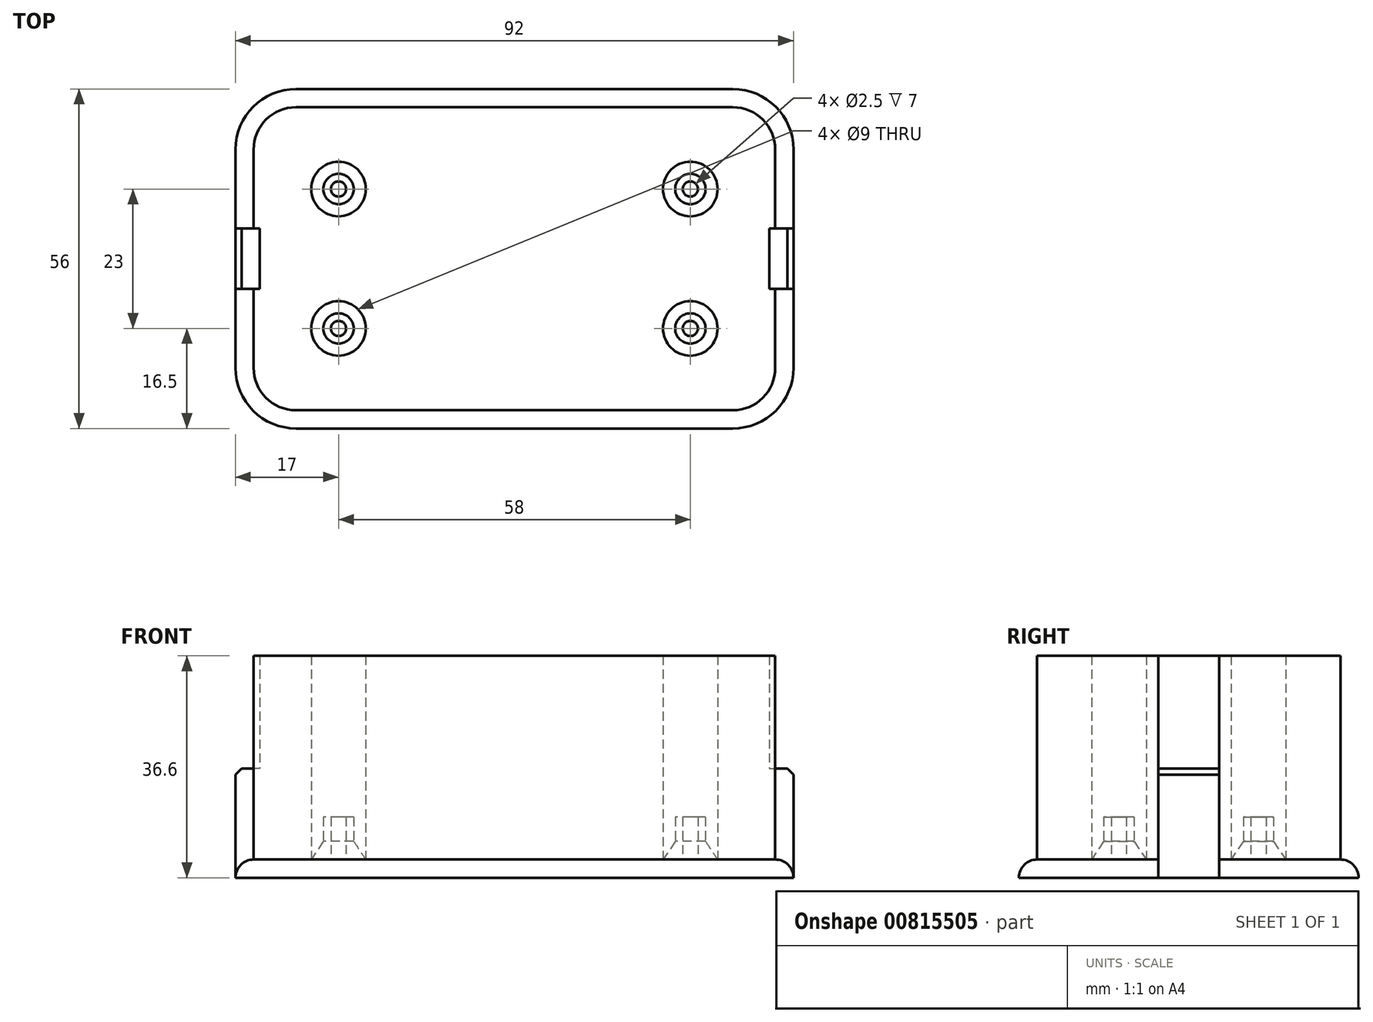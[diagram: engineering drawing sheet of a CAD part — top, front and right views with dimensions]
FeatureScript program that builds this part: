
annotation { "Feature Type Name" : "Feature", "Feature Type Description" : "" }
export const myFeature = defineFeature(function(context is Context, id is Id, definition is map)
    precondition{}
    {
        {
            var Q0;
            Q0=qCreatedBy(makeId("Top.planeOp"),FACE);
            var sketch = newSketch(context, id + "F0", { "sketchPlane" : qUnion([Q0])});
            skLineSegment(sketch, "E0.bottom", {"start": v(36, 28) * mm, "end": v(-36, 28) * mm});
            skLineSegment(sketch, "E0.top", {"start": v(36, -28) * mm, "end": v(-36, -28) * mm});
            skLineSegment(sketch, "E0.left", {"start": v(46, 18) * mm, "end": v(46, -18) * mm});
            skLineSegment(sketch, "E0.right", {"start": v(-46, 18) * mm, "end": v(-46, -18) * mm});
            skPoint(sketch, "E0.middle", {"position": v(0, 0) * mm});
            skPoint(sketch, "E1.visualSharp", {"position": v(-46, 28) * mm});
            skArc(sketch, "E1.filletArc", {"start": v(-36, 28) * mm, "mid": v(-43.07, 25.07) * mm, "end": v(-46, 18) * mm});
            skPoint(sketch, "E2.visualSharp", {"position": v(-46, -28) * mm});
            skArc(sketch, "E2.filletArc", {"start": v(-46, -18) * mm, "mid": v(-43.07, -25.07) * mm, "end": v(-36, -28) * mm});
            skPoint(sketch, "E3.visualSharp", {"position": v(46, -28) * mm});
            skArc(sketch, "E3.filletArc", {"start": v(36, -28) * mm, "mid": v(43.07, -25.07) * mm, "end": v(46, -18) * mm});
            skPoint(sketch, "E4.visualSharp", {"position": v(46, 28) * mm});
            skArc(sketch, "E4.filletArc", {"start": v(46, 18) * mm, "mid": v(43.07, 25.07) * mm, "end": v(36, 28) * mm});
            skSolve(sketch);
        }
        {
            var Q0;
            Q0=qCreatedBy(makeId("Top.planeOp"),FACE);
            var sketch = newSketch(context, id + "F1", { "sketchPlane" : qUnion([Q0])});
            skPoint(sketch, "E5", {"position": v(-32.5, 15) * mm});
            skPoint(sketch, "E6", {"position": v(32.5, 15) * mm});
            skPoint(sketch, "E7", {"position": v(32.5, -15) * mm});
            skPoint(sketch, "E8", {"position": v(-32.5, -15) * mm});
            skLineSegment(sketch, "E9", {"start": v(-29.5, 15) * mm, "end": v(29.5, 15) * mm, "construction": true});
            skLineSegment(sketch, "E10", {"start": v(32.5, 12) * mm, "end": v(32.5, -12) * mm, "construction": true});
            skLineSegment(sketch, "E11.MirrorCS", {"start": v(-29.5, -15) * mm, "end": v(29.5, -15) * mm, "construction": true});
            skLineSegment(sketch, "E12.MirrorCS", {"start": v(-32.5, 12) * mm, "end": v(-32.5, -12) * mm, "construction": true});
            skArc(sketch, "E13.filletArc", {"start": v(32.5, 12) * mm, "mid": v(31.62, 14.12) * mm, "end": v(29.5, 15) * mm, "construction": true});
            skArc(sketch, "E14.filletArc", {"start": v(-29.5, 15) * mm, "mid": v(-31.62, 14.12) * mm, "end": v(-32.5, 12) * mm, "construction": true});
            skArc(sketch, "E15.filletArc", {"start": v(-32.5, -12) * mm, "mid": v(-31.62, -14.12) * mm, "end": v(-29.5, -15) * mm, "construction": true});
            skArc(sketch, "E16.filletArc", {"start": v(29.5, -15) * mm, "mid": v(31.62, -14.12) * mm, "end": v(32.5, -12) * mm, "construction": true});
            skCircle(sketch, "E17", {"center": v(-29, 11.5) * mm, "radius": 1.25 * mm});
            skCircle(sketch, "E18.MirrorC", {"center": v(29, 11.5) * mm, "radius": 1.25 * mm});
            skCircle(sketch, "E19.MirrorC", {"center": v(-29, -11.5) * mm, "radius": 1.25 * mm});
            skCircle(sketch, "E20.MirrorC", {"center": v(29, -11.5) * mm, "radius": 1.25 * mm});
            skCircle(sketch, "E21", {"center": v(-29, 11.5) * mm, "radius": 2.5 * mm});
            skCircle(sketch, "E22.MirrorC", {"center": v(29, 11.5) * mm, "radius": 2.5 * mm});
            skCircle(sketch, "E23.MirrorC", {"center": v(-29, -11.5) * mm, "radius": 2.5 * mm});
            skCircle(sketch, "E24.MirrorC", {"center": v(29, -11.5) * mm, "radius": 2.5 * mm});
            skSolve(sketch);
        }
        {
            var Q0;
            Q0=makeQuery(id+"F0.imprint","IMPRINT",FACE,{"disambiguationData":[TD([[makeQuery(id+"F0.imprint","IMPRINT",EDGE,{"derivedFrom":sQuery(id+"F0.wireOp",EDGE,"E0.bottom")}),1.0]])]});
            extrude(context, id + "F2", {"entities" : qUnion([Q0]), "depth" : 3 * mm, "offsetDistance" : 25 * mm});
        }
        {
            var Q0;
            Q0=qSketchRegion(id+"F1",true);
            extrude(context, id + "F3", {"entities" : qUnion([Q0]), "operationType" : NewBodyOperationType.ADD, "depth" : 10 * mm, "offsetDistance" : 25 * mm});
        }
        {
            var Q0;
            Q0=makeQuery(id+"F3.boolean.opBoolean","INTERSECT",EDGE,{"derivedFrom":[makeQuery(id+"F2.opExtrude","CAP_FACE",FACE,{"disambiguationData":[OSD([sQuery(id+"F0.wireOp",EDGE,"E0.bottom"),sQuery(id+"F0.wireOp",EDGE,"E0.top"),sQuery(id+"F0.wireOp",EDGE,"E0.left"),sQuery(id+"F0.wireOp",EDGE,"E0.right"),sQuery(id+"F0.wireOp",EDGE,"E1.filletArc"),sQuery(id+"F0.wireOp",EDGE,"E2.filletArc"),sQuery(id+"F0.wireOp",EDGE,"E3.filletArc"),sQuery(id+"F0.wireOp",EDGE,"E4.filletArc")])],"isStart":false}),makeQuery(id+"F3.opExtrude","SWEPT_FACE",FACE,{"disambiguationData":[OSD([sQuery(id+"F1.wireOp",EDGE,"E21")])]})]});
            var Q1;
            Q1=makeQuery(id+"F3.boolean.opBoolean","INTERSECT",EDGE,{"derivedFrom":[makeQuery(id+"F2.opExtrude","CAP_FACE",FACE,{"disambiguationData":[OSD([sQuery(id+"F0.wireOp",EDGE,"E0.bottom"),sQuery(id+"F0.wireOp",EDGE,"E0.top"),sQuery(id+"F0.wireOp",EDGE,"E0.left"),sQuery(id+"F0.wireOp",EDGE,"E0.right"),sQuery(id+"F0.wireOp",EDGE,"E1.filletArc"),sQuery(id+"F0.wireOp",EDGE,"E2.filletArc"),sQuery(id+"F0.wireOp",EDGE,"E3.filletArc"),sQuery(id+"F0.wireOp",EDGE,"E4.filletArc")])],"isStart":false}),makeQuery(id+"F3.opExtrude","SWEPT_FACE",FACE,{"disambiguationData":[OSD([sQuery(id+"F1.wireOp",EDGE,"E22.MirrorC")])]})]});
            var Q2;
            Q2=makeQuery(id+"F3.boolean.opBoolean","INTERSECT",EDGE,{"derivedFrom":[makeQuery(id+"F2.opExtrude","CAP_FACE",FACE,{"disambiguationData":[OSD([sQuery(id+"F0.wireOp",EDGE,"E0.bottom"),sQuery(id+"F0.wireOp",EDGE,"E0.top"),sQuery(id+"F0.wireOp",EDGE,"E0.left"),sQuery(id+"F0.wireOp",EDGE,"E0.right"),sQuery(id+"F0.wireOp",EDGE,"E1.filletArc"),sQuery(id+"F0.wireOp",EDGE,"E2.filletArc"),sQuery(id+"F0.wireOp",EDGE,"E3.filletArc"),sQuery(id+"F0.wireOp",EDGE,"E4.filletArc")])],"isStart":false}),makeQuery(id+"F3.opExtrude","SWEPT_FACE",FACE,{"disambiguationData":[OSD([sQuery(id+"F1.wireOp",EDGE,"E24.MirrorC")])]})]});
            var Q3;
            Q3=makeQuery(id+"F3.boolean.opBoolean","INTERSECT",EDGE,{"derivedFrom":[makeQuery(id+"F2.opExtrude","CAP_FACE",FACE,{"disambiguationData":[OSD([sQuery(id+"F0.wireOp",EDGE,"E0.bottom"),sQuery(id+"F0.wireOp",EDGE,"E0.top"),sQuery(id+"F0.wireOp",EDGE,"E0.left"),sQuery(id+"F0.wireOp",EDGE,"E0.right"),sQuery(id+"F0.wireOp",EDGE,"E1.filletArc"),sQuery(id+"F0.wireOp",EDGE,"E2.filletArc"),sQuery(id+"F0.wireOp",EDGE,"E3.filletArc"),sQuery(id+"F0.wireOp",EDGE,"E4.filletArc")])],"isStart":false}),makeQuery(id+"F3.opExtrude","SWEPT_FACE",FACE,{"disambiguationData":[OSD([sQuery(id+"F1.wireOp",EDGE,"E23.MirrorC")])]})]});
            chamfer(context, id + "F4", {"entities" : qUnion([Q0, Q1, Q2, Q3]), "chamferType" : ChamferType.TWO_OFFSETS, "width1" : 2 * mm, "oppositeDirection" : false, "width2" : 3 * mm, "tangentPropagation" : true});
        }
        {
            var Q0;
            Q0=makeQuery(id+"F2.opExtrude","CAP_EDGE",EDGE,{"disambiguationData":[OSD([sQuery(id+"F0.wireOp",EDGE,"E0.bottom")])],"isStart":false});
            fillet(context, id + "F5", {"entities" : qUnion([Q0]), "radius" : 3 * mm, "tangentPropagation" : true, "allowEdgeOverflow" : false});
        }
        {
            var Q0;
            Q0=qCreatedBy(makeId("Right.planeOp"),FACE);
            cPlane(context, id + "F6", {"entities" : qUnion([Q0]), "cplaneType" : CPlaneType.OFFSET, "offset" : 46 * mm, "width" : 150 * mm, "height" : 150 * mm});
        }
        {
            var Q0;
            Q0=qCreatedBy(id+"F6.planeOp",FACE);
            var sketch = newSketch(context, id + "F7", { "sketchPlane" : qUnion([Q0])});
            skLineSegment(sketch, "E25", {"start": v(-5, 0) * mm, "end": v(-5, 18) * mm});
            skLineSegment(sketch, "E26", {"start": v(-5, 18) * mm, "end": v(5, 18) * mm});
            skLineSegment(sketch, "E27", {"start": v(5, 18) * mm, "end": v(5, 0) * mm});
            skLineSegment(sketch, "E28", {"start": v(-5, 0) * mm, "end": v(5, 0) * mm});
            skSolve(sketch);
        }
        {
            var Q0;
            Q0=makeQuery(id+"F7.imprint","IMPRINT",FACE,{"disambiguationData":[TD([[makeQuery(id+"F7.imprint","IMPRINT",EDGE,{"derivedFrom":sQuery(id+"F7.wireOp",EDGE,"E25")}),-1.0]])]});
            extrude(context, id + "F8", {"entities" : qUnion([Q0]), "oppositeDirection" : true, "depth" : 4 * mm, "offsetDistance" : 25 * mm});
        }
        {
            var Q0;
            Q0=makeQuery(id+"F8.opExtrude","SWEPT_BODY",BODY,{"disambiguationData":[OSD([sQuery(id+"F7.wireOp",EDGE,"E25"),sQuery(id+"F7.wireOp",EDGE,"E26"),sQuery(id+"F7.wireOp",EDGE,"E27"),sQuery(id+"F7.wireOp",EDGE,"E28")])]});
            var Q1;
            Q1=qCreatedBy(makeId("Right.planeOp"),FACE);
            mirror(context, id + "F9", {"operationType" : NewBodyOperationType.ADD, "entities" : qUnion([Q0]), "mirrorPlane" : qUnion([Q1])});
        }
        {
            var Q0;
            Q0=makeQuery(id+"F9.opPattern","COPY",EDGE,{"derivedFrom":makeQuery(id+"F8.opExtrude","CAP_EDGE",EDGE,{"disambiguationData":[OSD([sQuery(id+"F7.wireOp",EDGE,"E26")])],"isStart":true}),"instanceName":"1"});
            var Q1;
            Q1=makeQuery(id+"F8.opExtrude","CAP_EDGE",EDGE,{"disambiguationData":[OSD([sQuery(id+"F7.wireOp",EDGE,"E26")])],"isStart":true});
            chamfer(context, id + "F10", {"entities" : qUnion([Q0, Q1]), "width" : 1 * mm, "tangentPropagation" : true});
        }
        {
            var Q0;
            {var subQ0=sQuery(id+"F0.wireOp",EDGE,"E4.filletArc");var subQ1=sQuery(id+"F0.wireOp",EDGE,"E3.filletArc");var subQ2=sQuery(id+"F0.wireOp",EDGE,"E2.filletArc");var subQ3=sQuery(id+"F0.wireOp",EDGE,"E1.filletArc");var subQ4=sQuery(id+"F0.wireOp",EDGE,"E0.bottom");var subQ5=sQuery(id+"F0.wireOp",EDGE,"E0.right");var subQ6=sQuery(id+"F0.wireOp",EDGE,"E0.top");var subQ7=sQuery(id+"F0.wireOp",EDGE,"E0.left");Q0=makeQuery(id+"F3.boolean.opBoolean","SPLIT",FACE,{"disambiguationData":[TD([makeQuery(id+"F2.opExtrude","SWEPT_FACE",FACE,{"disambiguationData":[OSD([subQ4])]})])],"derivedFrom":makeQuery(id+"F2.opExtrude","CAP_FACE",FACE,{"disambiguationData":[OSD([subQ4,subQ6,subQ7,subQ5,subQ3,subQ2,subQ1,subQ0])],"isStart":false})});}
            extrude(context, id + "F11", {"entities" : qUnion([Q0]), "operationType" : NewBodyOperationType.ADD, "depth" : 33.6 * mm, "offsetDistance" : 25 * mm});
        }
    });
